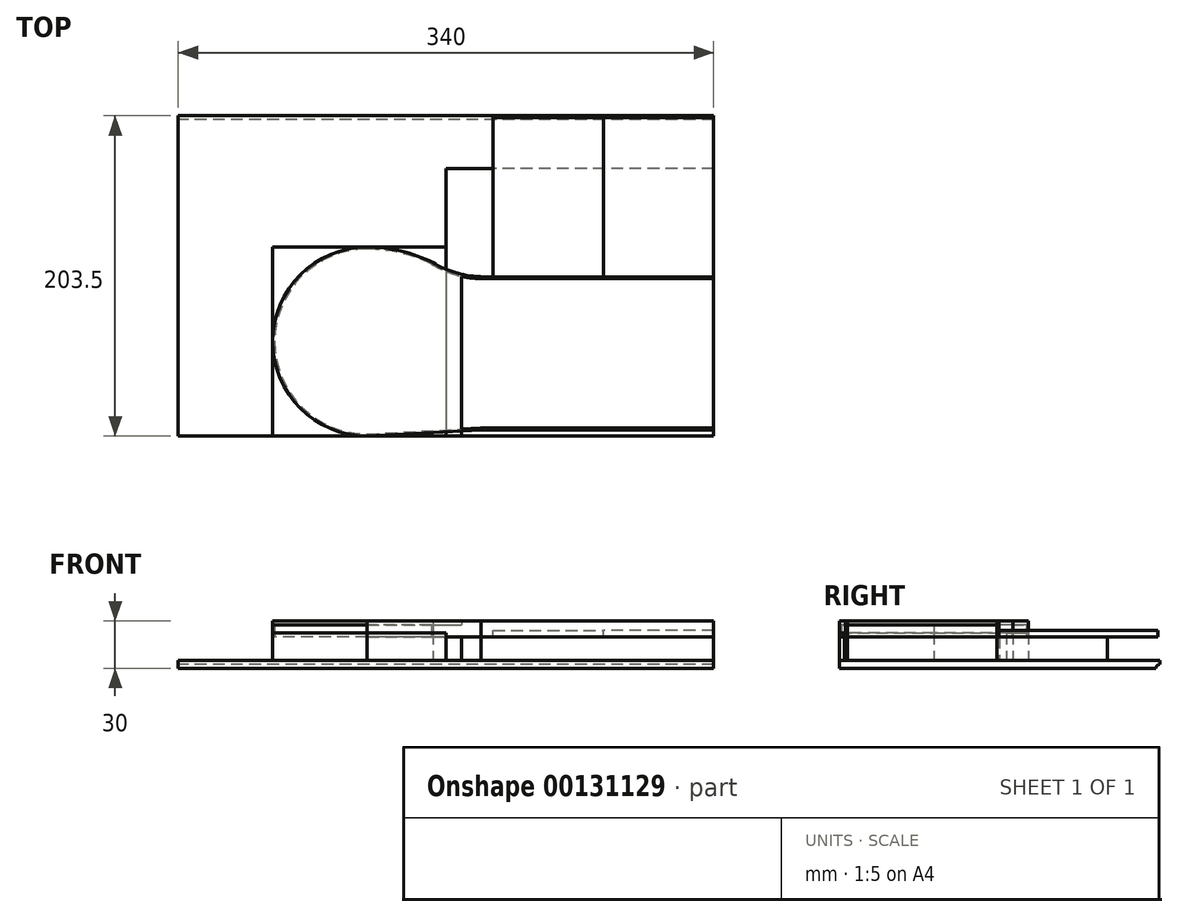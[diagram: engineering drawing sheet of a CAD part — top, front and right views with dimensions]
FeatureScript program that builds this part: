
annotation { "Feature Type Name" : "Feature", "Feature Type Description" : "" }
export const myFeature = defineFeature(function(context is Context, id is Id, definition is map)
    precondition{}
    {
        {
            var Q0;
            Q0=qCreatedBy(makeId("Right.planeOp"),FACE);
            var sketch = newSketch(context, id + "F0", { "sketchPlane" : qUnion([Q0])});
            skLineSegment(sketch, "E0", {"start": v(42.14, 7.34) * mm, "end": v(-129.14, 7.34) * mm});
            skLineSegment(sketch, "E1", {"start": v(-129.14, 7.34) * mm, "end": v(-129.14, 2.34) * mm});
            skLineSegment(sketch, "E2", {"start": v(-134.14, 7.34) * mm, "end": v(-129.14, 7.34) * mm});
            skLineSegment(sketch, "E3", {"start": v(-134.14, 7.34) * mm, "end": v(-134.14, 2.34) * mm});
            skLineSegment(sketch, "E4", {"start": v(-134.14, 2.34) * mm, "end": v(-129.14, 2.34) * mm});
            skLineSegment(sketch, "E5", {"start": v(74.36, 7.34) * mm, "end": v(74.36, 23.84) * mm});
            skLineSegment(sketch, "E6", {"start": v(74.36, 7.34) * mm, "end": v(74.36, 2.34) * mm});
            skLineSegment(sketch, "E7", {"start": v(42.14, 7.34) * mm, "end": v(74.36, 7.34) * mm});
            skLineSegment(sketch, "E8", {"start": v(-129.14, 2.34) * mm, "end": v(74.36, 2.34) * mm});
            skLineSegment(sketch, "E9", {"start": v(-129.14, 7.34) * mm, "end": v(-125.18, 7.34) * mm});
            skLineSegment(sketch, "E10", {"start": v(-125.18, 7.34) * mm, "end": v(-125.18, 9.84) * mm});
            skLineSegment(sketch, "E11", {"start": v(-125.18, 9.84) * mm, "end": v(-123.62, 9.84) * mm});
            skLineSegment(sketch, "E12", {"start": v(-123.62, 9.84) * mm, "end": v(-123.62, 7.34) * mm});
            skLineSegment(sketch, "E13", {"start": v(42.14, 7.34) * mm, "end": v(19.2, 7.34) * mm});
            skLineSegment(sketch, "E14", {"start": v(19.2, 7.34) * mm, "end": v(19.2, 9.84) * mm});
            skLineSegment(sketch, "E15", {"start": v(19.2, 9.84) * mm, "end": v(17.63, 9.84) * mm});
            skLineSegment(sketch, "E16", {"start": v(17.63, 9.84) * mm, "end": v(17.63, 7.34) * mm});
            skLineSegment(sketch, "E17", {"start": v(-125.18, 9.84) * mm, "end": v(-129.14, 9.84) * mm});
            skLineSegment(sketch, "E18.bottom", {"start": v(-129.14, 9.84) * mm, "end": v(40.86, 9.84) * mm});
            skLineSegment(sketch, "E18.top", {"start": v(-129.14, 12.34) * mm, "end": v(40.86, 12.34) * mm});
            skLineSegment(sketch, "E18.left", {"start": v(-129.14, 9.84) * mm, "end": v(-129.14, 12.34) * mm});
            skLineSegment(sketch, "E18.right", {"start": v(40.86, 9.84) * mm, "end": v(40.86, 12.34) * mm});
            skLineSegment(sketch, "E19", {"start": v(-134.14, 2.34) * mm, "end": v(-130.45, -11.44) * mm});
            skLineSegment(sketch, "E20", {"start": v(-125.18, -15.12) * mm, "end": v(-92.63, -12.27) * mm});
            skLineSegment(sketch, "E21", {"start": v(-88.4, -9.08) * mm, "end": v(-84.03, 2.34) * mm});
            skLineSegment(sketch, "E22", {"start": v(-84.03, 2.34) * mm, "end": v(-84.93, 0) * mm});
            skLineSegment(sketch, "E23", {"start": v(-84.03, 2.34) * mm, "end": v(-81.53, 2.34) * mm});
            skArc(sketch, "E24", {"start": v(-81.53, 2.34) * mm, "mid": v(-83.6, 1.7) * mm, "end": v(-84.93, 0) * mm});
            skLineSegment(sketch, "E25", {"start": v(-134.14, 2.34) * mm, "end": v(-128.96, 2.34) * mm});
            skLineSegment(sketch, "E26", {"start": v(-87.53, -6.8) * mm, "end": v(-93.07, -7.3) * mm});
            skLineSegment(sketch, "E27", {"start": v(-93.07, -7.3) * mm, "end": v(-130.67, -10.58) * mm});
            skLineSegment(sketch, "E28", {"start": v(-130.67, -10.58) * mm, "end": v(-125.62, -10.14) * mm});
            skLineSegment(sketch, "E29", {"start": v(-125.62, -10.14) * mm, "end": v(-128.96, 2.34) * mm});
            skPoint(sketch, "E30.visualSharp", {"position": v(-129.36, -15.49) * mm});
            skArc(sketch, "E30.filletArc", {"start": v(-130.45, -11.44) * mm, "mid": v(-128.48, -14.24) * mm, "end": v(-125.18, -15.12) * mm});
            skPoint(sketch, "E31.visualSharp", {"position": v(-89.51, -12) * mm});
            skArc(sketch, "E31.filletArc", {"start": v(-92.63, -12.27) * mm, "mid": v(-90.05, -11.28) * mm, "end": v(-88.4, -9.08) * mm});
            skLineSegment(sketch, "E32", {"start": v(-89.39, 2.34) * mm, "end": v(-93.07, -7.3) * mm});
            skLineSegment(sketch, "E33", {"start": v(-129.14, 12.34) * mm, "end": v(-116.64, 12.34) * mm});
            skLineSegment(sketch, "E34", {"start": v(-116.64, 12.34) * mm, "end": v(-116.64, 35.34) * mm});
            skLineSegment(sketch, "E35", {"start": v(-116.64, 35.34) * mm, "end": v(-21.64, 35.34) * mm});
            skLineSegment(sketch, "E36", {"start": v(-21.64, 35.34) * mm, "end": v(-21.64, 12.34) * mm});
            skCircle(sketch, "E37", {"center": v(74.36, 23.84) * mm, "radius": 16.5 * mm});
            skLineSegment(sketch, "E38", {"start": v(74.36, 40.34) * mm, "end": v(-129.14, 40.34) * mm});
            skLineSegment(sketch, "E39", {"start": v(-129.14, 40.34) * mm, "end": v(-129.14, 7.34) * mm});
            skLineSegment(sketch, "E40", {"start": v(74.36, 45.34) * mm, "end": v(-134.14, 45.34) * mm});
            skLineSegment(sketch, "E41", {"start": v(-134.14, 45.34) * mm, "end": v(-134.14, 7.34) * mm});
            skLineSegment(sketch, "E42", {"start": v(74.36, 23.84) * mm, "end": v(90.86, 23.84) * mm});
            skArc(sketch, "E43", {"start": v(74.36, 2.34) * mm, "mid": v(95.86, 23.84) * mm, "end": v(74.36, 45.34) * mm});
            skLineSegment(sketch, "E44", {"start": v(-129.14, 40.34) * mm, "end": v(-129.14, 45.34) * mm});
            skLineSegment(sketch, "E45", {"start": v(74.36, 7.34) * mm, "end": v(74.36, 4.84) * mm});
            skLineSegment(sketch, "E46", {"start": v(74.36, 2.34) * mm, "end": v(71.86, 2.34) * mm});
            skArc(sketch, "E47", {"start": v(74.36, 4.84) * mm, "mid": v(72.6, 4.1) * mm, "end": v(71.86, 2.34) * mm});
            skLineSegment(sketch, "E48", {"start": v(74.36, 4.84) * mm, "end": v(74.36, 2.34) * mm});
            skLineSegment(sketch, "E49.bottom", {"start": v(-129.14, 40.34) * mm, "end": v(-126.64, 40.34) * mm});
            skLineSegment(sketch, "E49.top", {"start": v(-129.14, 37.84) * mm, "end": v(-126.64, 37.84) * mm});
            skLineSegment(sketch, "E49.left", {"start": v(-129.14, 40.34) * mm, "end": v(-129.14, 37.84) * mm});
            skLineSegment(sketch, "E49.right", {"start": v(-126.64, 40.34) * mm, "end": v(-126.64, 37.84) * mm});
            skLineSegment(sketch, "E50", {"start": v(-129.14, 37.84) * mm, "end": v(-129.14, 35.34) * mm});
            skLineSegment(sketch, "E51", {"start": v(-129.14, 35.34) * mm, "end": v(-126.64, 37.84) * mm});
            skLineSegment(sketch, "E52", {"start": v(74.36, 45.34) * mm, "end": v(74.36, 43.67) * mm});
            skLineSegment(sketch, "E53", {"start": v(74.36, 43.67) * mm, "end": v(71.86, 43.67) * mm});
            skLineSegment(sketch, "E54", {"start": v(71.86, 43.67) * mm, "end": v(71.86, 42) * mm});
            skLineSegment(sketch, "E55", {"start": v(71.86, 42) * mm, "end": v(74.36, 42) * mm});
            skLineSegment(sketch, "E56", {"start": v(74.36, 42) * mm, "end": v(74.36, 40.34) * mm});
            skLineSegment(sketch, "E57", {"start": v(74.36, 23.84) * mm, "end": v(57.86, 23.84) * mm});
            skSolve(sketch);
        }
        {
            var Q0;
            {var subQ2=sQuery(id+"F0.wireOp",EDGE,"E1");Q0=makeQuery(id+"F0.imprint","IMPRINT",FACE,{"disambiguationData":[TD([[makeQuery(id+"F0.imprint","IMPRINT",EDGE,{"derivedFrom":subQ2}),1.0]])]});}
            extrude(context, id + "F1", {"entities" : qUnion([Q0]), "depth" : 170 * mm, "hasSecondDirection" : true, "secondDirectionOppositeDirection" : true, "secondDirectionDepth" : 170 * mm});
        }
        {
            var Q0;
            Q0=makeQuery(id+"F1.opExtrude","SWEPT_BODY",BODY,{"disambiguationData":[OSD([sQuery(id+"F0.wireOp",EDGE,"E0"),sQuery(id+"F0.wireOp",EDGE,"E1"),sQuery(id+"F0.wireOp",EDGE,"E7"),sQuery(id+"F0.wireOp",EDGE,"E8"),sQuery(id+"F0.wireOp",EDGE,"E9"),sQuery(id+"F0.wireOp",EDGE,"E13"),sQuery(id+"F0.wireOp",EDGE,"E23"),sQuery(id+"F0.wireOp",EDGE,"E25"),sQuery(id+"F0.wireOp",EDGE,"E45"),sQuery(id+"F0.wireOp",EDGE,"E47")])]});
            var Q1;
            Q1=qCreatedBy(makeId("Top.planeOp"),FACE);
            transform(context, id + "F2", {"entities" : qUnion([Q0]), "transformType" : TransformType.TRANSLATION_DISTANCE, "transformDirection" : qUnion([Q1]), "distance" : 75 * mm, "oppositeDirection" : true, "makeCopy" : false});
        }
        {
            var Q0;
            Q0=makeQuery(id+"F1.opExtrude","SWEPT_FACE",FACE,{"disambiguationData":[OSD([sQuery(id+"F0.wireOp",EDGE,"E0"),sQuery(id+"F0.wireOp",EDGE,"E7"),sQuery(id+"F0.wireOp",EDGE,"E9"),sQuery(id+"F0.wireOp",EDGE,"E13")])]});
            var sketch = newSketch(context, id + "F3", { "sketchPlane" : qUnion([Q0])});
            skLineSegment(sketch, "E58.bottom", {"start": v(170, -129.14) * mm, "end": v(0, -129.14) * mm});
            skLineSegment(sketch, "E58.top", {"start": v(170, 40.86) * mm, "end": v(0, 40.86) * mm});
            skLineSegment(sketch, "E58.left", {"start": v(170, -129.14) * mm, "end": v(170, 40.86) * mm});
            skLineSegment(sketch, "E59", {"start": v(0, -129.14) * mm, "end": v(10, -129.14) * mm});
            skLineSegment(sketch, "E60", {"start": v(170, -129.14) * mm, "end": v(170, -124.13) * mm});
            skLineSegment(sketch, "E61.bottom", {"start": v(10, -129.14) * mm, "end": v(-110, -129.14) * mm});
            skLineSegment(sketch, "E61.left", {"start": v(10, -129.14) * mm, "end": v(10, -9.14) * mm});
            skLineSegment(sketch, "E61.right", {"start": v(-110, -129.14) * mm, "end": v(-110, -9.14) * mm});
            skLineSegment(sketch, "E62.left", {"start": v(170, -124.13) * mm, "end": v(170, -29.25) * mm});
            skLineSegment(sketch, "E63", {"start": v(170, 40.86) * mm, "end": v(170, 74.36) * mm});
            skLineSegment(sketch, "E64", {"start": v(170, 74.36) * mm, "end": v(-170, 74.36) * mm});
            skLineSegment(sketch, "E65", {"start": v(0, 40.86) * mm, "end": v(170, 40.86) * mm});
            skLineSegment(sketch, "E66.bottom", {"start": v(170, 74.36) * mm, "end": v(24, 74.36) * mm});
            skLineSegment(sketch, "E66.top", {"start": v(170, -26.64) * mm, "end": v(24, -26.64) * mm});
            skLineSegment(sketch, "E66.left", {"start": v(170, 74.36) * mm, "end": v(170, -26.64) * mm});
            skLineSegment(sketch, "E66.right", {"start": v(24, 74.36) * mm, "end": v(24, -26.64) * mm});
            skLineSegment(sketch, "E67", {"start": v(22.08, -124.13) * mm, "end": v(170, -124.13) * mm});
            skPoint(sketch, "E68.endSnap0", {"position": v(-50, -129.14) * mm});
            skLineSegment(sketch, "E69", {"start": v(-50, -127.89) * mm, "end": v(-50, -129.14) * mm});
            skLineSegment(sketch, "E70", {"start": v(-50, -10.39) * mm, "end": v(-50, -9.14) * mm});
            skPoint(sketch, "E71.endSnap0", {"position": v(-110, -69.14) * mm});
            skLineSegment(sketch, "E72", {"start": v(-108.75, -69.14) * mm, "end": v(-110, -69.14) * mm});
            skArc(sketch, "E73", {"start": v(-50, -9.14) * mm, "mid": v(-110, -69.14) * mm, "end": v(-50, -129.14) * mm});
            skArc(sketch, "E74", {"start": v(-8.3, -18.94) * mm, "mid": v(7.23, -25.69) * mm, "end": v(24, -28) * mm});
            skLineSegment(sketch, "E75", {"start": v(170, -29.25) * mm, "end": v(24, -29.25) * mm});
            skLineSegment(sketch, "E76", {"start": v(24, -28) * mm, "end": v(170, -28) * mm});
            skArc(sketch, "E77", {"start": v(-8.3, -18.94) * mm, "mid": v(-28.6, -11.66) * mm, "end": v(-50, -9.14) * mm});
            skArc(sketch, "E78", {"start": v(-9.18, -19.82) * mm, "mid": v(-29.07, -12.83) * mm, "end": v(-50, -10.39) * mm});
            skArc(sketch, "E79", {"start": v(-9.18, -19.82) * mm, "mid": v(6.75, -26.84) * mm, "end": v(24, -29.25) * mm});
            skLineSegment(sketch, "E80", {"start": v(-50, -127.89) * mm, "end": v(22.08, -124.13) * mm});
            skLineSegment(sketch, "E81", {"start": v(22.15, -125.38) * mm, "end": v(-50, -129.14) * mm});
            skLineSegment(sketch, "E82", {"start": v(22.15, -125.38) * mm, "end": v(170, -125.38) * mm});
            skLineSegment(sketch, "E83", {"start": v(-110, -129.14) * mm, "end": v(-170, -129.14) * mm});
            skLineSegment(sketch, "E84", {"start": v(-170, -129.14) * mm, "end": v(-170, 74.36) * mm});
            skLineSegment(sketch, "E85", {"start": v(10, -9.14) * mm, "end": v(-110, -9.14) * mm});
            skLineSegment(sketch, "E86", {"start": v(0, 40.86) * mm, "end": v(0, -129.14) * mm});
            skArc(sketch, "E87", {"start": v(-50, -10.39) * mm, "mid": v(-108.75, -69.14) * mm, "end": v(-50, -127.89) * mm});
            skSolve(sketch);
        }
        {
            var Q0;
            {var subQ4=sQuery(id+"F3.wireOp",EDGE,"E58.bottom");Q0=makeQuery(id+"F3.imprint","IMPRINT",FACE,{"disambiguationData":[TD([[makeQuery(id+"F3.imprint","IMPRINT",EDGE,{"derivedFrom":subQ4}),-1.0]])]});}
            var Q1;
            {var subQ1=sQuery(id+"F3.wireOp",EDGE,"E67");Q1=makeQuery(id+"F3.imprint","IMPRINT",FACE,{"disambiguationData":[TD([[makeQuery(id+"F3.imprint","IMPRINT",EDGE,{"derivedFrom":subQ1}),-1.0]])]});}
            var Q2;
            {var subQ0=sQuery(id+"F3.wireOp",EDGE,"E81");var subQ1=sQuery(id+"F3.wireOp",EDGE,"E61.left");var subQ2=makeQuery(id+"F3.imprint","INTERSECT",VERTEX,{"derivedFrom":[subQ1,subQ0]});Q2=makeQuery(id+"F3.imprint","IMPRINT",FACE,{"disambiguationData":[TD([[makeQuery(id+"F3.imprint","IMPRINT",EDGE,{"disambiguationData":[TD([[subQ2,-1.0]])],"derivedFrom":subQ1}),1.0]])]});}
            var Q3;
            {var subQ0=sQuery(id+"F3.wireOp",EDGE,"E61.left");var subQ5=sQuery(id+"F3.wireOp",EDGE,"E81");var subQ6=makeQuery(id+"F3.imprint","INTERSECT",VERTEX,{"derivedFrom":[subQ0,subQ5]});Q3=makeQuery(id+"F3.imprint","IMPRINT",FACE,{"disambiguationData":[TD([[makeQuery(id+"F3.imprint","IMPRINT",EDGE,{"disambiguationData":[TD([[subQ6,-1.0]])],"derivedFrom":subQ5}),1.0]])]});}
            var Q4;
            {var subQ0=sQuery(id+"F3.wireOp",EDGE,"E79");var subQ1=sQuery(id+"F3.wireOp",EDGE,"E61.left");var subQ2=makeQuery(id+"F3.imprint","INTERSECT",VERTEX,{"derivedFrom":[subQ1,subQ0]});Q4=makeQuery(id+"F3.imprint","IMPRINT",FACE,{"disambiguationData":[TD([[makeQuery(id+"F3.imprint","IMPRINT",EDGE,{"disambiguationData":[TD([[subQ2,-1.0]])],"derivedFrom":subQ1}),1.0]])]});}
            var Q5;
            {var subQ0=sQuery(id+"F3.wireOp",EDGE,"E80");var subQ1=sQuery(id+"F3.wireOp",EDGE,"E61.left");var subQ2=makeQuery(id+"F3.imprint","INTERSECT",VERTEX,{"derivedFrom":[subQ1,subQ0]});Q5=makeQuery(id+"F3.imprint","IMPRINT",FACE,{"disambiguationData":[TD([[makeQuery(id+"F3.imprint","IMPRINT",EDGE,{"disambiguationData":[TD([[subQ2,-1.0]])],"derivedFrom":subQ1}),1.0]])]});}
            var Q6;
            {var subQ0=sQuery(id+"F3.wireOp",EDGE,"E75");Q6=makeQuery(id+"F3.imprint","IMPRINT",FACE,{"disambiguationData":[TD([[makeQuery(id+"F3.imprint","IMPRINT",EDGE,{"derivedFrom":subQ0}),-1.0]])]});}
            var Q7;
            Q7=makeQuery(id+"F3.imprint","IMPRINT",FACE,{"disambiguationData":[TD([[makeQuery(id+"F3.imprint","IMPRINT",EDGE,{"derivedFrom":sQuery(id+"F3.wireOp",EDGE,"E62.left")}),-1.0]])]});
            var Q8;
            {var subQ0=sQuery(id+"F3.wireOp",EDGE,"E85");var subQ1=sQuery(id+"F3.wireOp",EDGE,"E61.left");var subQ2=makeQuery(id+"F3.imprint","INTERSECT",VERTEX,{"derivedFrom":[subQ1,subQ0]});Q8=makeQuery(id+"F3.imprint","IMPRINT",FACE,{"disambiguationData":[TD([[makeQuery(id+"F3.imprint","IMPRINT",EDGE,{"disambiguationData":[TD([[subQ2,1.0]])],"derivedFrom":subQ1}),1.0]])]});}
            var Q9;
            {var subQ5=sQuery(id+"F3.wireOp",EDGE,"E66.top");Q9=makeQuery(id+"F3.imprint","IMPRINT",FACE,{"disambiguationData":[TD([[makeQuery(id+"F3.imprint","IMPRINT",EDGE,{"derivedFrom":subQ5}),-1.0]])]});}
            var Q10;
            {var subQ5=sQuery(id+"F3.wireOp",EDGE,"E66.top");Q10=makeQuery(id+"F3.imprint","IMPRINT",FACE,{"disambiguationData":[TD([[makeQuery(id+"F3.imprint","IMPRINT",EDGE,{"derivedFrom":subQ5}),1.0]])]});}
            extrude(context, id + "F4", {"entities" : qUnion([Q0, Q1, Q2, Q3, Q4, Q5, Q6, Q7, Q8, Q9, Q10]), "depth" : 15 * mm});
        }
        {
            var Q0;
            {var subQ0=sQuery(id+"F3.wireOp",EDGE,"E77");Q0=makeQuery(id+"F3.imprint","IMPRINT",FACE,{"disambiguationData":[TD([[makeQuery(id+"F3.imprint","IMPRINT",EDGE,{"derivedFrom":subQ0}),-1.0]])]});}
            var Q1;
            {var subQ0=sQuery(id+"F3.wireOp",EDGE,"E85");var subQ1=sQuery(id+"F3.wireOp",EDGE,"E61.right");var subQ2=makeQuery(id+"F3.imprint","INTERSECT",VERTEX,{"derivedFrom":[subQ1,subQ0]});Q1=makeQuery(id+"F3.imprint","IMPRINT",FACE,{"disambiguationData":[TD([[makeQuery(id+"F3.imprint","IMPRINT",EDGE,{"disambiguationData":[TD([[subQ2,1.0]])],"derivedFrom":subQ1}),-1.0]])]});}
            var Q2;
            {var subQ0=sQuery(id+"F3.wireOp",EDGE,"E61.right");var subQ1=sQuery(id+"F3.wireOp",EDGE,"E61.bottom");var subQ2=makeQuery(id+"F3.imprint","INTERSECT",VERTEX,{"derivedFrom":[subQ1,subQ0,sQuery(id+"F3.wireOp",EDGE,"E83")]});Q2=makeQuery(id+"F3.imprint","IMPRINT",FACE,{"disambiguationData":[TD([[makeQuery(id+"F3.imprint","IMPRINT",EDGE,{"disambiguationData":[TD([[subQ2,-1.0]])],"derivedFrom":subQ0}),-1.0]])]});}
            var Q3;
            {var subQ1=sQuery(id+"F3.wireOp",EDGE,"E61.bottom");var subQ3=sQuery(id+"F3.wireOp",EDGE,"E86");var subQ4=makeQuery(id+"F3.imprint","INTERSECT",VERTEX,{"derivedFrom":[subQ1,subQ3]});Q3=makeQuery(id+"F3.imprint","IMPRINT",FACE,{"disambiguationData":[TD([[makeQuery(id+"F3.imprint","IMPRINT",EDGE,{"disambiguationData":[TD([[subQ4,1.0]])],"derivedFrom":subQ3}),-1.0]])]});}
            extrude(context, id + "F5", {"entities" : qUnion([Q0, Q1, Q2, Q3]), "depth" : 17.5 * mm});
        }
        {
            var Q0;
            Q0=makeQuery(id+"F5.opExtrude","CAP_FACE",FACE,{"disambiguationData":[OSD([sQuery(id+"F3.wireOp",EDGE,"E61.bottom"),sQuery(id+"F3.wireOp",EDGE,"E61.right"),sQuery(id+"F3.wireOp",EDGE,"E73")])],"isStart":false});
            var Q1;
            Q1=makeQuery(id+"F5.opExtrude","CAP_FACE",FACE,{"disambiguationData":[OSD([sQuery(id+"F3.wireOp",EDGE,"E61.right"),sQuery(id+"F3.wireOp",EDGE,"E73"),sQuery(id+"F3.wireOp",EDGE,"E85")])],"isStart":false});
            extrude(context, id + "F6", {"entities" : qUnion([Q0, Q1]), "depth" : 5 * mm});
        }
        {
            var Q0;
            Q0=makeQuery(id+"F3.imprint","IMPRINT",FACE,{"disambiguationData":[TD([[makeQuery(id+"F3.imprint","IMPRINT",EDGE,{"derivedFrom":sQuery(id+"F3.wireOp",EDGE,"E70")}),-1.0]])]});
            var Q1;
            {var subQ0=sQuery(id+"F3.wireOp",EDGE,"E70");Q1=makeQuery(id+"F3.imprint","IMPRINT",FACE,{"disambiguationData":[TD([[makeQuery(id+"F3.imprint","IMPRINT",EDGE,{"derivedFrom":subQ0}),1.0]])]});}
            var Q2;
            {var subQ0=sQuery(id+"F3.wireOp",EDGE,"E69");Q2=makeQuery(id+"F3.imprint","IMPRINT",FACE,{"disambiguationData":[TD([[makeQuery(id+"F3.imprint","IMPRINT",EDGE,{"derivedFrom":subQ0}),-1.0]])]});}
            var Q3;
            {var subQ0=sQuery(id+"F3.wireOp",EDGE,"E69");Q3=makeQuery(id+"F3.imprint","IMPRINT",FACE,{"disambiguationData":[TD([[makeQuery(id+"F3.imprint","IMPRINT",EDGE,{"derivedFrom":subQ0}),1.0]])]});}
            var Q4;
            {var subQ0=sQuery(id+"F3.wireOp",EDGE,"E79");var subQ1=sQuery(id+"F3.wireOp",EDGE,"E61.left");var subQ2=makeQuery(id+"F3.imprint","INTERSECT",VERTEX,{"derivedFrom":[subQ1,subQ0]});Q4=makeQuery(id+"F3.imprint","IMPRINT",FACE,{"disambiguationData":[TD([[makeQuery(id+"F3.imprint","IMPRINT",EDGE,{"disambiguationData":[TD([[subQ2,-1.0]])],"derivedFrom":subQ1}),1.0]])]});}
            var Q5;
            {var subQ0=sQuery(id+"F3.wireOp",EDGE,"E75");Q5=makeQuery(id+"F3.imprint","IMPRINT",FACE,{"disambiguationData":[TD([[makeQuery(id+"F3.imprint","IMPRINT",EDGE,{"derivedFrom":subQ0}),-1.0]])]});}
            var Q6;
            {var subQ0=sQuery(id+"F3.wireOp",EDGE,"E81");var subQ1=sQuery(id+"F3.wireOp",EDGE,"E61.left");var subQ2=makeQuery(id+"F3.imprint","INTERSECT",VERTEX,{"derivedFrom":[subQ1,subQ0]});Q6=makeQuery(id+"F3.imprint","IMPRINT",FACE,{"disambiguationData":[TD([[makeQuery(id+"F3.imprint","IMPRINT",EDGE,{"disambiguationData":[TD([[subQ2,-1.0]])],"derivedFrom":subQ1}),1.0]])]});}
            var Q7;
            {var subQ1=sQuery(id+"F3.wireOp",EDGE,"E67");Q7=makeQuery(id+"F3.imprint","IMPRINT",FACE,{"disambiguationData":[TD([[makeQuery(id+"F3.imprint","IMPRINT",EDGE,{"derivedFrom":subQ1}),-1.0]])]});}
            extrude(context, id + "F7", {"entities" : qUnion([Q0, Q1, Q2, Q3, Q4, Q5, Q6, Q7]), "depth" : 25 * mm, "hasSecondDirection" : true, "secondDirectionOppositeDirection" : false, "secondDirectionDepth" : 15 * mm});
        }
        {
            var Q0;
            {var subQ6=sQuery(id+"F3.wireOp",EDGE,"E78");Q0=makeQuery(id+"F3.imprint","IMPRINT",FACE,{"disambiguationData":[TD([[makeQuery(id+"F3.imprint","IMPRINT",EDGE,{"derivedFrom":subQ6}),1.0]])]});}
            var Q1;
            {var subQ0=sQuery(id+"F3.wireOp",EDGE,"E80");var subQ1=sQuery(id+"F3.wireOp",EDGE,"E61.left");var subQ2=makeQuery(id+"F3.imprint","INTERSECT",VERTEX,{"derivedFrom":[subQ1,subQ0]});Q1=makeQuery(id+"F3.imprint","IMPRINT",FACE,{"disambiguationData":[TD([[makeQuery(id+"F3.imprint","IMPRINT",EDGE,{"disambiguationData":[TD([[subQ2,-1.0]])],"derivedFrom":subQ1}),1.0]])]});}
            var Q2;
            Q2=makeQuery(id+"F3.imprint","IMPRINT",FACE,{"disambiguationData":[TD([[makeQuery(id+"F3.imprint","IMPRINT",EDGE,{"derivedFrom":sQuery(id+"F3.wireOp",EDGE,"E62.left")}),-1.0]])]});
            extrude(context, id + "F8", {"entities" : qUnion([Q0, Q1, Q2]), "operationType" : NewBodyOperationType.ADD, "depth" : 25 * mm, "hasSecondDirection" : true, "secondDirectionOppositeDirection" : false, "secondDirectionDepth" : 22.5 * mm});
        }
        {
            var Q0;
            {var subQ0=sQuery(id+"F3.wireOp",EDGE,"E87");var subQ1=sQuery(id+"F3.wireOp",EDGE,"E80");var subQ2=sQuery(id+"F3.wireOp",EDGE,"E79");var subQ3=sQuery(id+"F3.wireOp",EDGE,"E78");var subQ4=sQuery(id+"F3.wireOp",EDGE,"E75");var subQ5=sQuery(id+"F3.wireOp",EDGE,"E67");Q0=makeQuery(id+"F8.boolean.opBoolean","MERGE",FACE,{"derivedFrom":[makeQuery(id+"F7.opExtrude","CAP_FACE",FACE,{"disambiguationData":[OSD([sQuery(id+"F3.wireOp",EDGE,"E58.left"),sQuery(id+"F3.wireOp",EDGE,"E60"),subQ5,sQuery(id+"F3.wireOp",EDGE,"E73"),sQuery(id+"F3.wireOp",EDGE,"E74"),subQ4,sQuery(id+"F3.wireOp",EDGE,"E76"),sQuery(id+"F3.wireOp",EDGE,"E77"),subQ3,subQ2,subQ1,sQuery(id+"F3.wireOp",EDGE,"E81"),sQuery(id+"F3.wireOp",EDGE,"E82"),subQ0])],"isStart":false}),makeQuery(id+"F8.opExtrude","CAP_FACE",FACE,{"disambiguationData":[OSD([sQuery(id+"F3.wireOp",EDGE,"E62.left"),subQ5,subQ4,subQ3,subQ2,subQ1,subQ0])],"isStart":false})]});}
            var sketch = newSketch(context, id + "F9", { "sketchPlane" : qUnion([Q0])});
            skLineSegment(sketch, "E88.bottom", {"start": v(170, -28) * mm, "end": v(100, -28) * mm});
            skLineSegment(sketch, "E88.top", {"start": v(170, 73) * mm, "end": v(100, 73) * mm});
            skLineSegment(sketch, "E88.left", {"start": v(170, -28) * mm, "end": v(170, 73) * mm});
            skLineSegment(sketch, "E88.right", {"start": v(100, -28) * mm, "end": v(100, 73) * mm});
            skLineSegment(sketch, "E89.bottom", {"start": v(100, -28) * mm, "end": v(30, -28) * mm});
            skLineSegment(sketch, "E89.top", {"start": v(100, 73) * mm, "end": v(30, 73) * mm});
            skLineSegment(sketch, "E89.right", {"start": v(30, -28) * mm, "end": v(30, 73) * mm});
            skSolve(sketch);
        }
        {
            var Q0;
            Q0=makeQuery(id+"F9.imprint","IMPRINT",FACE,{"disambiguationData":[TD([[makeQuery(id+"F9.imprint","IMPRINT",EDGE,{"derivedFrom":sQuery(id+"F9.wireOp",EDGE,"E88.bottom")}),1.0]])]});
            extrude(context, id + "F10", {"entities" : qUnion([Q0]), "oppositeDirection" : true, "depth" : 10 * mm, "hasSecondDirection" : true, "secondDirectionOppositeDirection" : true, "secondDirectionDepth" : 6 * mm});
        }
        {
            var Q0;
            Q0=makeQuery(id+"F9.imprint","IMPRINT",FACE,{"disambiguationData":[TD([[makeQuery(id+"F9.imprint","IMPRINT",EDGE,{"derivedFrom":sQuery(id+"F9.wireOp",EDGE,"E89.bottom")}),1.0]])]});
            extrude(context, id + "F11", {"entities" : qUnion([Q0]), "oppositeDirection" : true, "depth" : 10 * mm, "hasSecondDirection" : true, "secondDirectionOppositeDirection" : true, "secondDirectionDepth" : 6 * mm});
        }
    });
